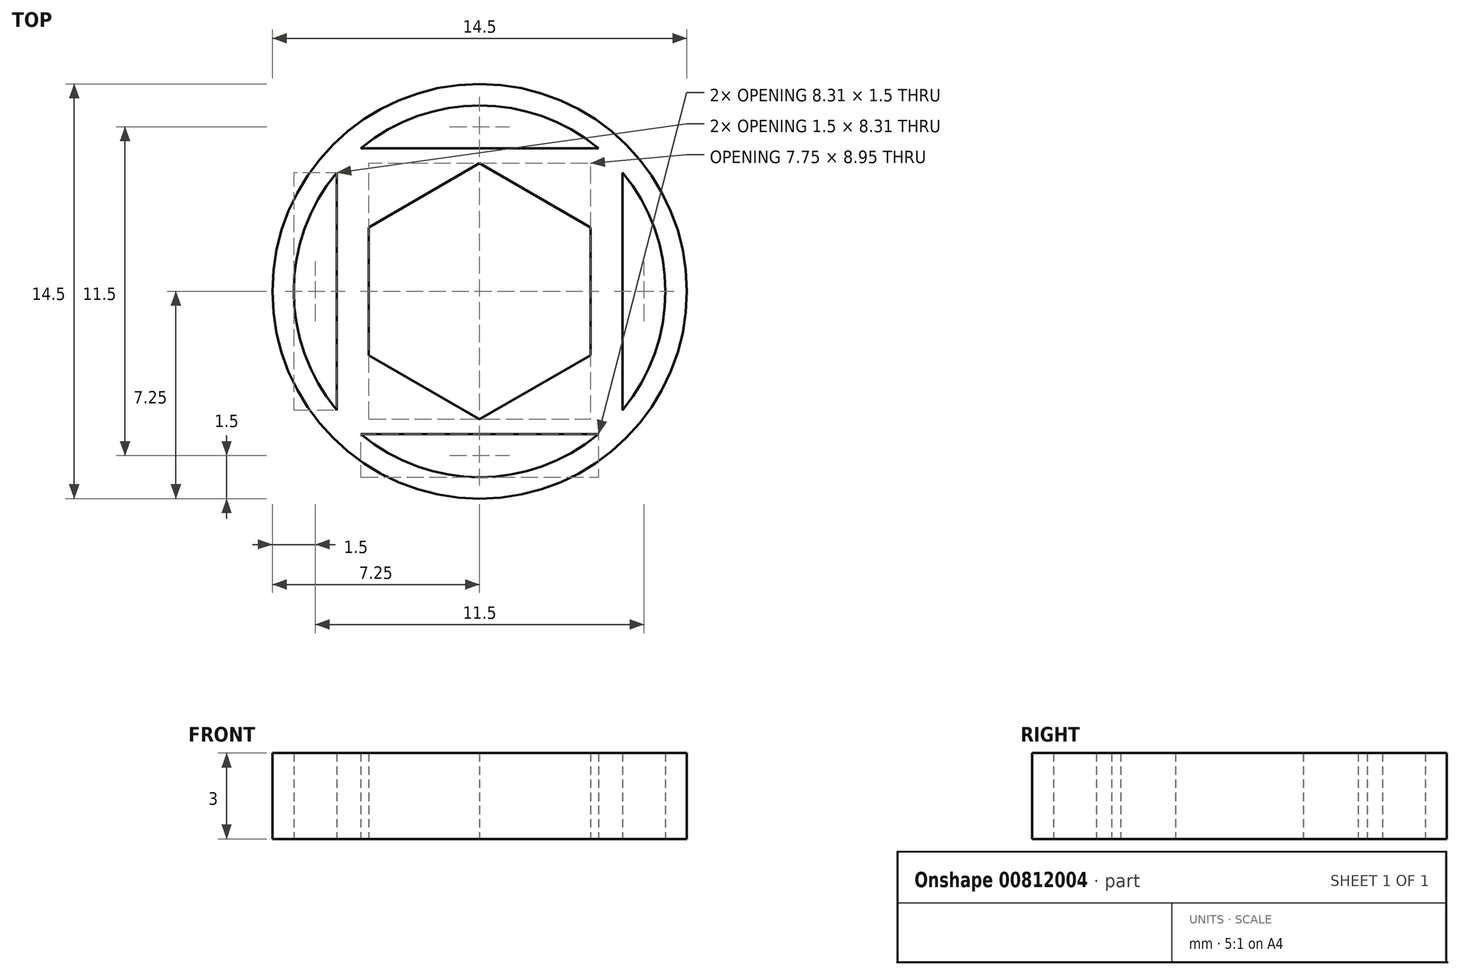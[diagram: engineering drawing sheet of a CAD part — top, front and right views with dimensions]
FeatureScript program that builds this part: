
annotation { "Feature Type Name" : "Feature", "Feature Type Description" : "" }
export const myFeature = defineFeature(function(context is Context, id is Id, definition is map)
    precondition{}
    {
        {
            var Q0;
            Q0=qCreatedBy(makeId("Top.planeOp"),FACE);
            var sketch = newSketch(context, id + "F0", { "sketchPlane" : qUnion([Q0])});
            skCircle(sketch, "E0.cCircle", {"center": v(0, 0) * mm, "radius": 3.88 * mm, "construction": true});
            skLineSegment(sketch, "E0.0", {"start": v(3.88, 2.24) * mm, "end": v(3.88, -2.24) * mm});
            skLineSegment(sketch, "E0.1", {"start": v(3.88, -2.24) * mm, "end": v(0, -4.47) * mm});
            skLineSegment(sketch, "E0.2", {"start": v(0, -4.47) * mm, "end": v(-3.88, -2.24) * mm});
            skLineSegment(sketch, "E0.3", {"start": v(-3.87, -2.24) * mm, "end": v(-3.88, 2.24) * mm});
            skLineSegment(sketch, "E0.4", {"start": v(-3.88, 2.24) * mm, "end": v(0, 4.47) * mm});
            skLineSegment(sketch, "E0.5", {"start": v(0, 4.47) * mm, "end": v(3.88, 2.24) * mm});
            skPoint(sketch, "E0.0.midPoint", {"position": v(3.88, 0) * mm});
            skLineSegment(sketch, "E1.bottom", {"start": v(5, 5) * mm, "end": v(-5, 5) * mm});
            skLineSegment(sketch, "E1.top", {"start": v(5, -5) * mm, "end": v(-5, -5) * mm});
            skLineSegment(sketch, "E1.left", {"start": v(5, 5) * mm, "end": v(5, -5) * mm});
            skLineSegment(sketch, "E1.right", {"start": v(-5, 5) * mm, "end": v(-5, -5) * mm});
            skCircle(sketch, "E2", {"center": v(0, 0) * mm, "radius": 6.5 * mm});
            skCircle(sketch, "E3", {"center": v(0, 0) * mm, "radius": 7.25 * mm});
            skSolve(sketch);
        }
        {
            var Q0;
            Q0=makeQuery(id+"F0.imprint","IMPRINT",FACE,{"disambiguationData":[TD([[makeQuery(id+"F0.imprint","IMPRINT",EDGE,{"derivedFrom":sQuery(id+"F0.wireOp",EDGE,"E3")}),1.0]])]});
            var Q1;
            Q1=makeQuery(id+"F0.imprint","IMPRINT",FACE,{"disambiguationData":[TD([[makeQuery(id+"F0.imprint","IMPRINT",EDGE,{"derivedFrom":sQuery(id+"F0.wireOp",EDGE,"E0.0")}),1.0]])]});
            var Q2;
            {var subQ0=sQuery(id+"F0.wireOp",EDGE,"E1.right");var subQ1=sQuery(id+"F0.wireOp",EDGE,"E1.bottom");var subQ2=makeQuery(id+"F0.imprint","INTERSECT",VERTEX,{"derivedFrom":[subQ1,subQ0]});Q2=makeQuery(id+"F0.imprint","IMPRINT",FACE,{"disambiguationData":[TD([[makeQuery(id+"F0.imprint","IMPRINT",EDGE,{"disambiguationData":[TD([[subQ2,1.0]])],"derivedFrom":subQ1}),1.0]])]});}
            var Q3;
            {var subQ0=sQuery(id+"F0.wireOp",EDGE,"E1.left");var subQ1=sQuery(id+"F0.wireOp",EDGE,"E1.bottom");var subQ2=makeQuery(id+"F0.imprint","INTERSECT",VERTEX,{"derivedFrom":[subQ1,subQ0]});Q3=makeQuery(id+"F0.imprint","IMPRINT",FACE,{"disambiguationData":[TD([[makeQuery(id+"F0.imprint","IMPRINT",EDGE,{"disambiguationData":[TD([[subQ2,-1.0]])],"derivedFrom":subQ1}),1.0]])]});}
            var Q4;
            {var subQ0=sQuery(id+"F0.wireOp",EDGE,"E1.left");var subQ1=sQuery(id+"F0.wireOp",EDGE,"E1.top");var subQ2=makeQuery(id+"F0.imprint","INTERSECT",VERTEX,{"derivedFrom":[subQ1,subQ0]});Q4=makeQuery(id+"F0.imprint","IMPRINT",FACE,{"disambiguationData":[TD([[makeQuery(id+"F0.imprint","IMPRINT",EDGE,{"disambiguationData":[TD([[subQ2,-1.0]])],"derivedFrom":subQ1}),-1.0]])]});}
            var Q5;
            {var subQ0=sQuery(id+"F0.wireOp",EDGE,"E1.right");var subQ1=sQuery(id+"F0.wireOp",EDGE,"E1.top");var subQ2=makeQuery(id+"F0.imprint","INTERSECT",VERTEX,{"derivedFrom":[subQ1,subQ0]});Q5=makeQuery(id+"F0.imprint","IMPRINT",FACE,{"disambiguationData":[TD([[makeQuery(id+"F0.imprint","IMPRINT",EDGE,{"disambiguationData":[TD([[subQ2,1.0]])],"derivedFrom":subQ1}),-1.0]])]});}
            extrude(context, id + "F1", {"entities" : qUnion([Q0, Q1, Q2, Q3, Q4, Q5]), "depth" : 3 * mm, "offsetDistance" : 25 * mm});
        }
    });
